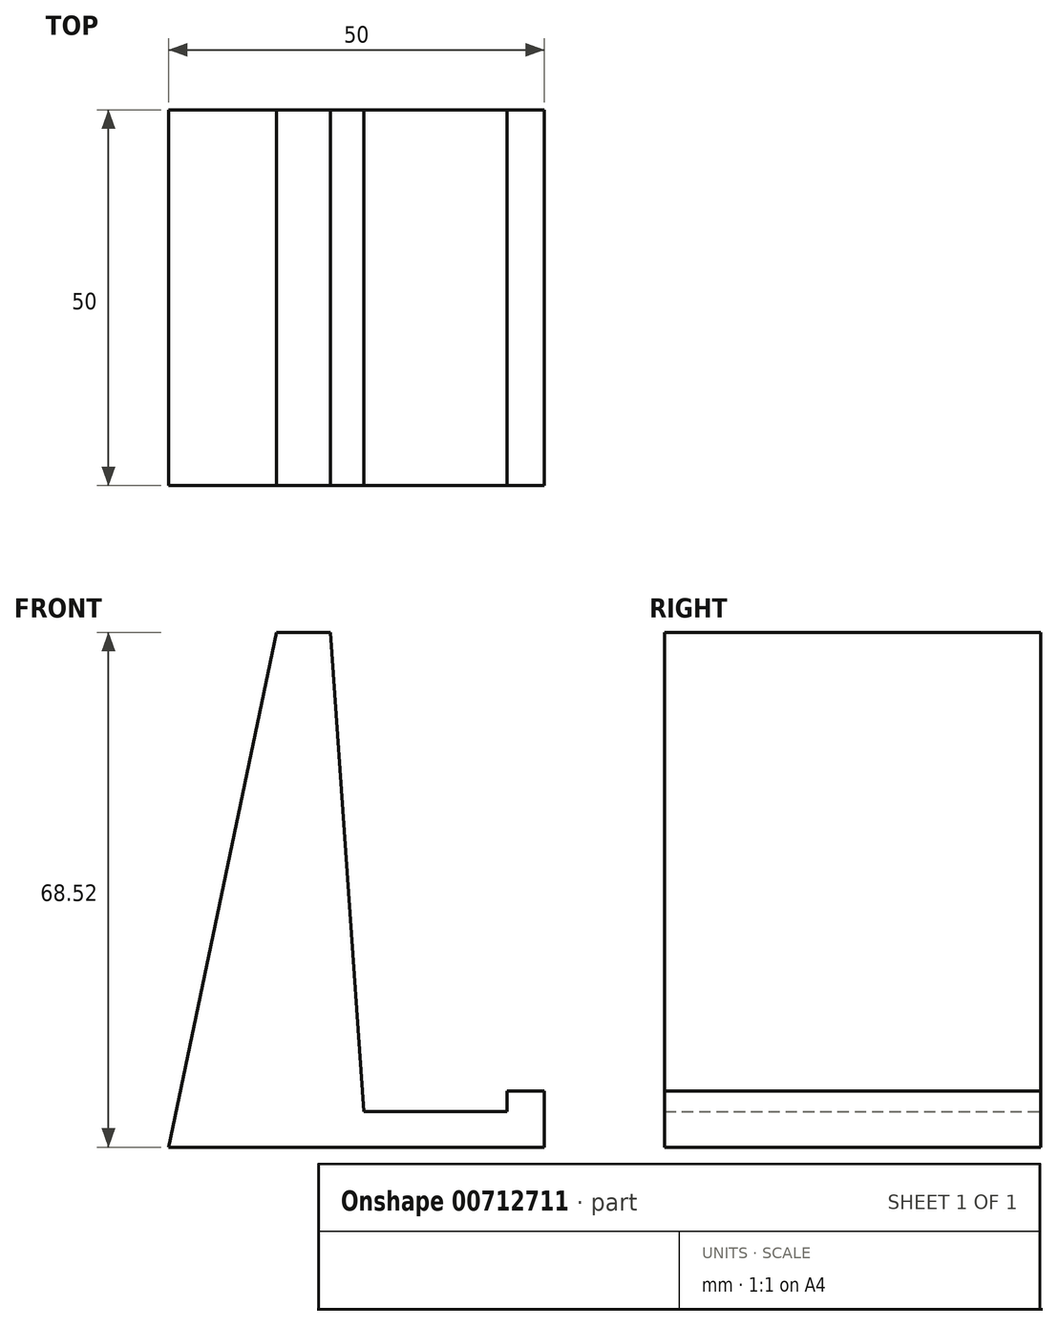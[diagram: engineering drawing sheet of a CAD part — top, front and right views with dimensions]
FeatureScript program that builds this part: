
annotation { "Feature Type Name" : "Feature", "Feature Type Description" : "" }
export const myFeature = defineFeature(function(context is Context, id is Id, definition is map)
    precondition{}
    {
        {
            var Q0;
            Q0=qCreatedBy(makeId("Front.planeOp"),FACE);
            var sketch = newSketch(context, id + "F0", { "sketchPlane" : qUnion([Q0])});
            skLineSegment(sketch, "E0", {"start": v(-30.58, 0) * mm, "end": v(-16.25, 68.52) * mm});
            skLineSegment(sketch, "E1", {"start": v(-30.58, 0) * mm, "end": v(19.42, 0) * mm});
            skLineSegment(sketch, "E2", {"start": v(19.42, 0) * mm, "end": v(19.42, 7.5) * mm});
            skLineSegment(sketch, "E3", {"start": v(19.42, 7.5) * mm, "end": v(14.42, 7.5) * mm});
            skLineSegment(sketch, "E4", {"start": v(14.42, 7.5) * mm, "end": v(14.42, 4.75) * mm});
            skLineSegment(sketch, "E5", {"start": v(14.42, 4.75) * mm, "end": v(-4.58, 4.75) * mm});
            skLineSegment(sketch, "E6", {"start": v(-4.58, 4.75) * mm, "end": v(-9.05, 68.52) * mm});
            skLineSegment(sketch, "E7", {"start": v(-16.25, 68.52) * mm, "end": v(-9.05, 68.52) * mm});
            skSolve(sketch);
        }
        {
            var Q0;
            Q0=makeQuery(id+"F0.imprint","IMPRINT",FACE,{"disambiguationData":[TD([[makeQuery(id+"F0.imprint","IMPRINT",EDGE,{"derivedFrom":sQuery(id+"F0.wireOp",EDGE,"E0")}),-1.0]])]});
            extrude(context, id + "F1", {"entities" : qUnion([Q0]), "depth" : 50 * mm, "offsetDistance" : 25 * mm});
        }
    });
